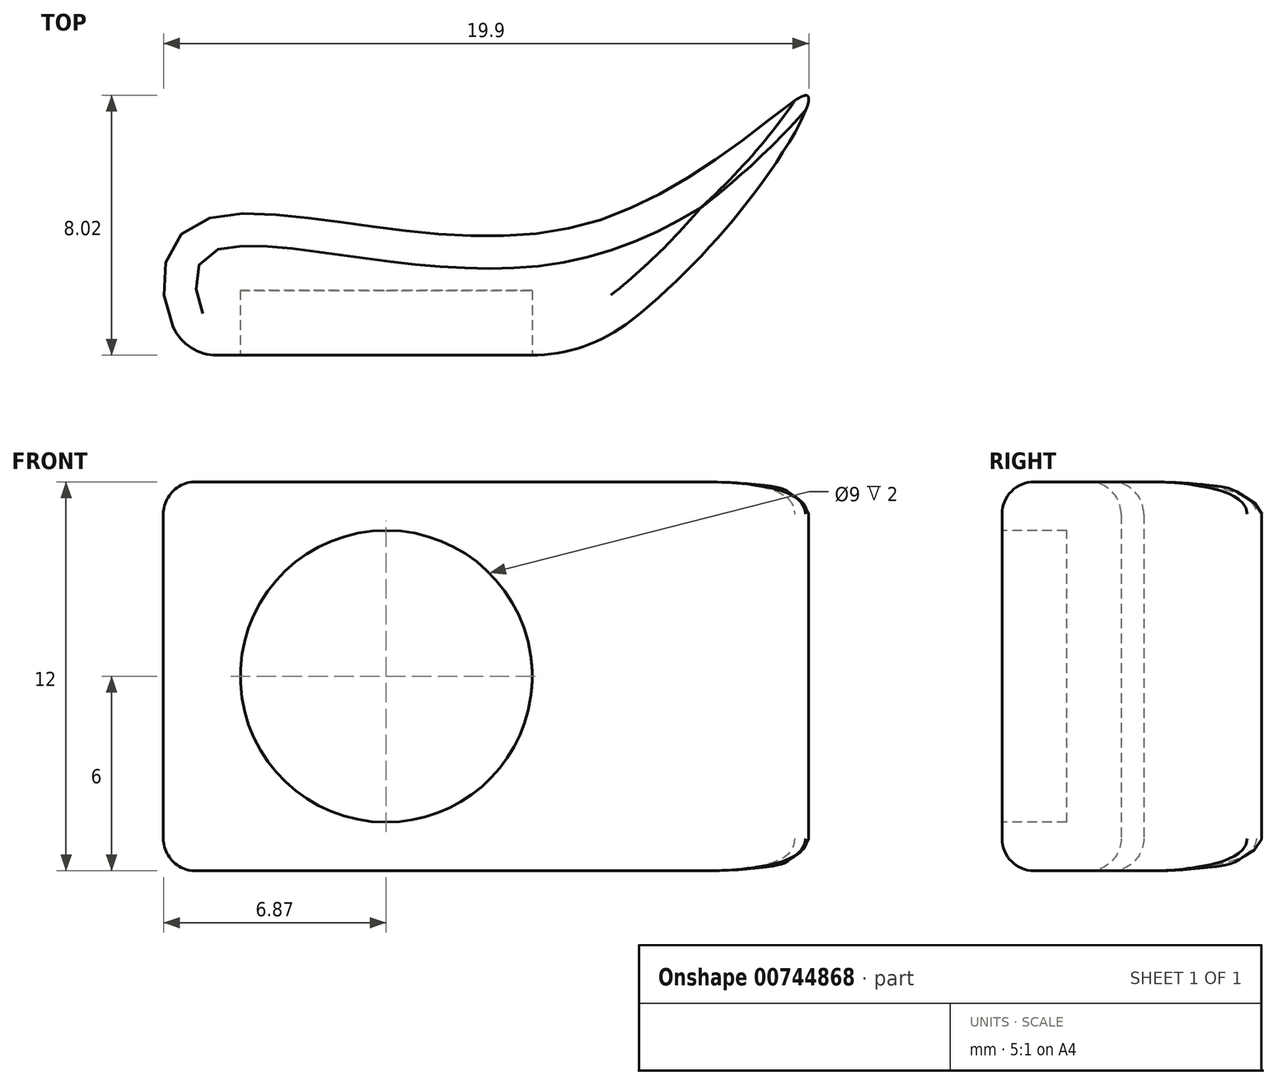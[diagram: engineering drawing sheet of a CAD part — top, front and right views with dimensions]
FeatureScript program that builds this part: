
annotation { "Feature Type Name" : "Feature", "Feature Type Description" : "" }
export const myFeature = defineFeature(function(context is Context, id is Id, definition is map)
    precondition{}
    {
        {
            var Q0;
            Q0=qCreatedBy(makeId("Top.planeOp"),FACE);
            var sketch = newSketch(context, id + "F0", { "sketchPlane" : qUnion([Q0])});
            skFitSpline(sketch, "E0", {"points": [v(0, 0) * mm, v(12, 0) * mm, v(19, 8) * mm, v(12, 4) * mm, v(0, 4) * mm, v(0, 0) * mm]});
            skLineSegment(sketch, "E1", {"start": v(0, 0) * mm, "end": v(12, 0) * mm});
            skSolve(sketch);
        }
        {
            var Q0;
            {var subQ0=sQuery(id+"F0.wireOp",EDGE,"E1");Q0=makeQuery(id+"F0.imprint","IMPRINT",FACE,{"disambiguationData":[TD([[makeQuery(id+"F0.imprint","IMPRINT",EDGE,{"derivedFrom":subQ0}),1.0]])]});}
            extrude(context, id + "F1", {"entities" : qUnion([Q0]), "depth" : 12 * mm, "offsetDistance" : 25 * mm});
        }
        {
            var Q0;
            Q0=makeQuery(id+"F1.opExtrude","SWEPT_FACE",FACE,{"disambiguationData":[OSD([sQuery(id+"F0.wireOp",EDGE,"E1")])]});
            var sketch = newSketch(context, id + "F2", { "sketchPlane" : qUnion([Q0])});
            skCircle(sketch, "E2", {"center": v(6, 6) * mm, "radius": 4.5 * mm});
            skPoint(sketch, "E2.centerSnap0", {"position": v(0, 6) * mm});
            skPoint(sketch, "E2.centerSnap1", {"position": v(6, 12) * mm});
            skSolve(sketch);
        }
        {
            var Q0;
            Q0=makeQuery(id+"F2.imprint","IMPRINT",FACE,{"disambiguationData":[TD([[makeQuery(id+"F2.imprint","IMPRINT",EDGE,{"derivedFrom":sQuery(id+"F2.wireOp",EDGE,"E2")}),1.0]])]});
            extrude(context, id + "F3", {"entities" : qUnion([Q0]), "operationType" : NewBodyOperationType.REMOVE, "oppositeDirection" : true, "depth" : 2 * mm, "offsetDistance" : 25 * mm});
        }
        {
            var Q0;
            {var subQ0=sQuery(id+"F0.wireOp",EDGE,"E1");var subQ1=sQuery(id+"F0.wireOp",EDGE,"E0");Q0=makeQuery(id+"F1.opExtrude","SWEPT_EDGE",EDGE,{"disambiguationData":[OSD([subQ1,subQ0]),TDD([makeQuery(id+"F0.imprint","INTERSECT",VERTEX,{"disambiguationData":[OD(1.0)],"derivedFrom":[subQ1,subQ0]})])]});}
            fillet(context, id + "F4", {"entities" : qUnion([Q0]), "radius" : 5 * mm, "tangentPropagation" : true, "allowEdgeOverflow" : false});
        }
        {
            var Q0;
            {var subQ0=sQuery(id+"F0.wireOp",EDGE,"E1");var subQ1=sQuery(id+"F0.wireOp",EDGE,"E0");Q0=makeQuery(id+"F1.opExtrude","SWEPT_EDGE",EDGE,{"disambiguationData":[OSD([subQ1,subQ0]),TDD([makeQuery(id+"F0.imprint","INTERSECT",VERTEX,{"disambiguationData":[OD(0.0)],"derivedFrom":[subQ1,subQ0]})])]});}
            fillet(context, id + "F5", {"entities" : qUnion([Q0]), "radius" : 1.5 * mm, "tangentPropagation" : true, "allowEdgeOverflow" : false});
        }
        {
            var Q0;
            Q0=makeQuery(id+"F1.opExtrude","CAP_EDGE",EDGE,{"disambiguationData":[OSD([sQuery(id+"F0.wireOp",EDGE,"E0")])],"isStart":false});
            var Q1;
            Q1=makeQuery(id+"F1.opExtrude","CAP_EDGE",EDGE,{"disambiguationData":[OSD([sQuery(id+"F0.wireOp",EDGE,"E0")])],"isStart":true});
            fillet(context, id + "F6", {"entities" : qUnion([Q0, Q1]), "radius" : 1 * mm, "tangentPropagation" : true, "allowEdgeOverflow" : false});
        }
    });
